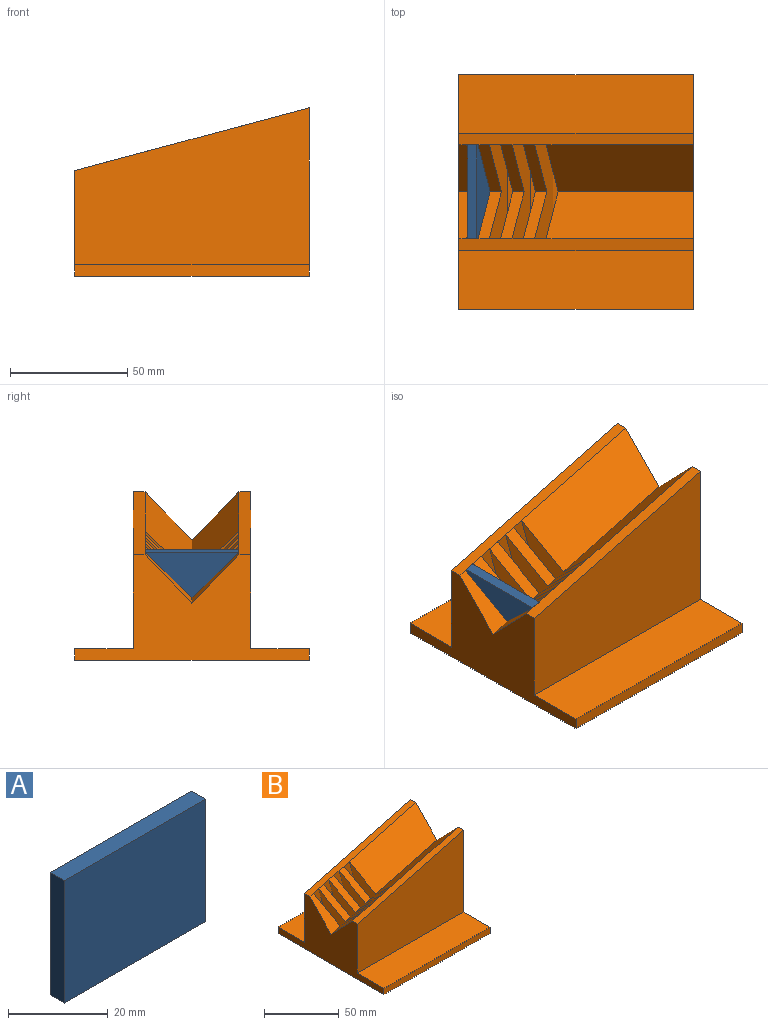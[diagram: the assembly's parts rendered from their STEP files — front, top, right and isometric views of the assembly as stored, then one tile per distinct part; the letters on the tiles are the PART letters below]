
ASSEMBLY  parts=2 mates=1
PART A: 6 faces, bbox 40x4x30 mm
  f0: plane 40x4mm, normal (0,0,-1), area 160mm2, adj f1,f3,f4,f5
  f1: plane 30x4mm, normal (1,0,0), area 120mm2, adj f0,f2,f4,f5
  f2: plane 40x4mm, normal (0,0,1), area 160mm2, adj f1,f3,f4,f5
  f3: plane 30x4mm, normal (-1,0,0), area 120mm2, adj f0,f2,f4,f5
  f4: plane 40x30mm, normal (0,-1,0), area 1200mm2, adj f0,f1,f2,f3
  f5: plane 40x30mm, normal (0,1,0), area 1200mm2, adj f0,f1,f2,f3
PART B: 41 faces, bbox 100x100x71.8 mm
  f0: plane 62.79x36.14mm, normal (-0.18,0.71,0.68), area 1762.7mm2, adj f1,f6,f23,f25
  f1: plane 62.79x36.14mm, normal (-0.18,-0.71,0.68), area 1762.7mm2, adj f0,f6,f25,f26
  f2: plane 40x4.83mm, normal (-0.26,0,0.97), area 200mm2, adj f3,f4,f5,f6
  f3: plane 30.27x12.59mm, normal (0,-1,0), area 150mm2, adj f2,f5,f6,f26
  f4: plane 30.27x12.59mm, normal (0,1,0), area 150mm2, adj f2,f5,f6,f23
  f5: plane 40x28.98mm, normal (0.97,0,0.26), area 800mm2, adj f2,f3,f4,f7,f8
  f6: plane 40x28.98mm, normal (-0.97,0,-0.26), area 800mm2, adj f0,f1,f2,f3,f4
  f7: plane 20.61x20mm, normal (-0.18,0.71,0.68), area 141.4mm2, adj f5,f8,f13,f23
  f8: plane 20.61x20mm, normal (-0.18,-0.71,0.68), area 141.4mm2, adj f5,f7,f13,f26
  f9: plane 40x4.83mm, normal (-0.26,0,0.97), area 200mm2, adj f10,f11,f12,f13
  f10: plane 30.27x12.59mm, normal (0,-1,0), area 150mm2, adj f9,f12,f13,f26
  f11: plane 30.27x12.59mm, normal (0,1,0), area 150mm2, adj f9,f12,f13,f23
  f12: plane 40x28.98mm, normal (0.97,0,0.26), area 800mm2, adj f9,f10,f11,f14,f15
  f13: plane 40x28.98mm, normal (-0.97,0,-0.26), area 800mm2, adj f7,f8,f9,f10,f11
  f14: plane 20.61x20mm, normal (-0.18,0.71,0.68), area 141.4mm2, adj f12,f15,f20,f23
  f15: plane 20.61x20mm, normal (-0.18,-0.71,0.68), area 141.4mm2, adj f12,f14,f20,f26
  f16: plane 40x4.83mm, normal (-0.26,0,0.97), area 200mm2, adj f17,f18,f19,f20
  f17: plane 30.27x12.59mm, normal (0,-1,0), area 150mm2, adj f16,f19,f20,f26
  f18: plane 30.27x12.59mm, normal (0,1,0), area 150mm2, adj f16,f19,f20,f23
  f19: plane 40x28.98mm, normal (0.97,0,0.26), area 800mm2, adj f16,f17,f18,f29,f30
  f20: plane 40x28.98mm, normal (-0.97,0,-0.26), area 800mm2, adj f14,f15,f16,f17,f18
  f21: plane 21.62x20mm, normal (-0.18,0.71,0.68), area 175.6mm2, adj f22,f23,f24,f35
  f22: plane 21.62x20mm, normal (-0.18,-0.71,0.68), area 175.6mm2, adj f21,f24,f26,f35
  f23: plane 100x26.8mm, normal (-0.26,0,0.97), area 517.6mm2, adj f0,f4,f7,f11,f14,f18,f21,f24
  f24: plane 100x45mm, normal (-1,0,0), area 2085.9mm2, adj f21,f22,f23,f26,f27,f28,f36,f37
  f25: plane 100x71.8mm, normal (1,0,0), area 3425.6mm2, adj f0,f1,f23,f26,f27,f28,f36,f37
  f26: plane 100x26.8mm, normal (-0.26,0,0.97), area 517.6mm2, adj f1,f3,f8,f10,f15,f17,f22,f24
  f27: plane 100x66.8mm, normal (0,-1,0), area 5339.7mm2, adj f23,f24,f25,f36
  f28: plane 100x66.8mm, normal (0,1,0), area 5339.7mm2, adj f24,f25,f26,f40
  f29: plane 20.61x20mm, normal (-0.18,0.71,0.68), area 141.4mm2, adj f19,f23,f30,f34
  f30: plane 20.61x20mm, normal (-0.18,-0.71,0.68), area 141.4mm2, adj f19,f26,f29,f34
  f31: plane 40x4.83mm, normal (-0.26,0,0.97), area 200mm2, adj f32,f33,f34,f35
  f32: plane 30.27x12.59mm, normal (0,-1,0), area 150mm2, adj f26,f31,f34,f35
  f33: plane 30.27x12.59mm, normal (0,1,0), area 150mm2, adj f23,f31,f34,f35
  f34: plane 40x28.98mm, normal (-0.97,0,-0.26), area 800mm2, adj f29,f30,f31,f32,f33
  f35: plane 40x28.98mm, normal (0.97,0,0.26), area 800mm2, adj f21,f22,f31,f32,f33
  f36: plane 100x25mm, normal (0,0,1), area 2500mm2, adj f24,f25,f27,f37
  f37: plane 100x5mm, normal (0,-1,0), area 500mm2, adj f24,f25,f36,f39
  f38: plane 100x5mm, normal (0,1,0), area 500mm2, adj f24,f25,f39,f40
  f39: plane 100x100mm, normal (0,0,-1), area 10000mm2, adj f24,f25,f37,f38
  f40: plane 100x25mm, normal (0,0,1), area 2500mm2, adj f24,f25,f28,f38
PLACE A rot(axis=(0.13,-0.13,-0.98),91deg) t=(-38.36,0,7.59)mm
PLACE B at identity fixed
MATE slider A.f0 <-> B.f31  axis (0.26,0,-0.97) through (-36.41,0,-7.42)mm
